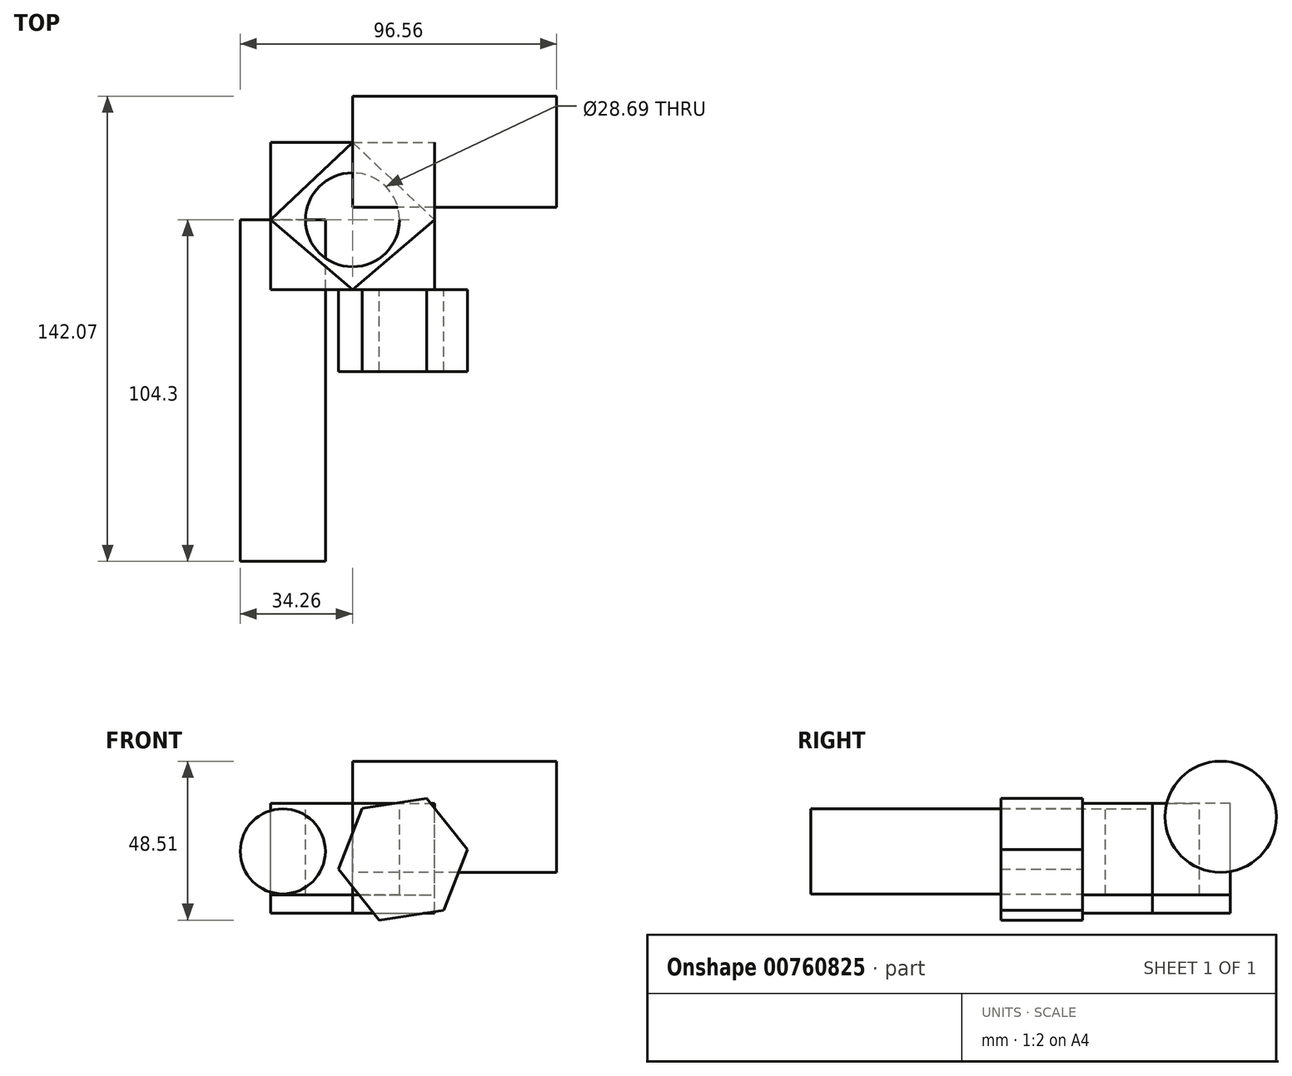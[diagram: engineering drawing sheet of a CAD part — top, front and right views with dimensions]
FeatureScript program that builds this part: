
annotation { "Feature Type Name" : "Feature", "Feature Type Description" : "" }
export const myFeature = defineFeature(function(context is Context, id is Id, definition is map)
    precondition{}
    {
        {
            var Q0;
            Q0=qCreatedBy(makeId("Top.planeOp"),FACE);
            var sketch = newSketch(context, id + "F0", { "sketchPlane" : qUnion([Q0])});
            skLineSegment(sketch, "E0.bottom", {"start": v(-25, 23.69) * mm, "end": v(25, 23.69) * mm});
            skLineSegment(sketch, "E0.top", {"start": v(-25, -21.31) * mm, "end": v(25, -21.31) * mm});
            skLineSegment(sketch, "E0.left", {"start": v(-25, 23.69) * mm, "end": v(-25, -21.31) * mm});
            skLineSegment(sketch, "E0.right", {"start": v(25, 23.69) * mm, "end": v(25, -21.31) * mm});
            skLineSegment(sketch, "E1", {"start": v(0, 23.69) * mm, "end": v(-25, 0) * mm});
            skLineSegment(sketch, "E2", {"start": v(-25, 0) * mm, "end": v(0, -21.31) * mm});
            skLineSegment(sketch, "E3", {"start": v(0, -21.31) * mm, "end": v(25, 0) * mm});
            skLineSegment(sketch, "E4", {"start": v(0, 23.69) * mm, "end": v(25, 0) * mm});
            skCircle(sketch, "E5", {"center": v(0, 0) * mm, "radius": 14.35 * mm});
            skSolve(sketch);
        }
        {
            var Q0;
            {var subQ3=sQuery(id+"F0.wireOp",EDGE,"E1");Q0=makeQuery(id+"F0.imprint","IMPRINT",FACE,{"disambiguationData":[TD([[makeQuery(id+"F0.imprint","IMPRINT",EDGE,{"derivedFrom":subQ3}),-1.0]])]});}
            var Q1;
            {var subQ3=sQuery(id+"F0.wireOp",EDGE,"E4");Q1=makeQuery(id+"F0.imprint","IMPRINT",FACE,{"disambiguationData":[TD([[makeQuery(id+"F0.imprint","IMPRINT",EDGE,{"derivedFrom":subQ3}),1.0]])]});}
            var Q2;
            {var subQ3=sQuery(id+"F0.wireOp",EDGE,"E2");Q2=makeQuery(id+"F0.imprint","IMPRINT",FACE,{"disambiguationData":[TD([[makeQuery(id+"F0.imprint","IMPRINT",EDGE,{"derivedFrom":subQ3}),-1.0]])]});}
            var Q3;
            {var subQ3=sQuery(id+"F0.wireOp",EDGE,"E3");Q3=makeQuery(id+"F0.imprint","IMPRINT",FACE,{"disambiguationData":[TD([[makeQuery(id+"F0.imprint","IMPRINT",EDGE,{"derivedFrom":subQ3}),-1.0]])]});}
            extrude(context, id + "F1", {"entities" : qUnion([Q0, Q1, Q2, Q3]), "oppositeDirection" : true, "depth" : 33.6 * mm, "offsetDistance" : 25 * mm});
        }
        {
            var Q0;
            Q0 = qSketchRegion(id + "F0", true);
            extrude(context, id + "F2", {"entities" : qUnion([Q0]), "oppositeDirection" : true, "depth" : 27.9 * mm, "offsetDistance" : 25 * mm});
        }
        {
            var Q0;
            Q0=qCreatedBy(makeId("Right.planeOp"),FACE);
            var sketch = newSketch(context, id + "F3", { "sketchPlane" : qUnion([Q0])});
            skCircle(sketch, "E6", {"center": v(20.79, -4.12) * mm, "radius": 16.98 * mm});
            skSolve(sketch);
        }
        {
            var Q0;
            Q0 = qSketchRegion(id + "F3", true);
            extrude(context, id + "F4", {"entities" : qUnion([Q0]), "depth" : 62.3 * mm, "offsetDistance" : 25 * mm});
        }
        {
            var Q0;
            Q0=qCreatedBy(makeId("Front.planeOp"),FACE);
            var sketch = newSketch(context, id + "F5", { "sketchPlane" : qUnion([Q0])});
            skCircle(sketch, "E7", {"center": v(-21.27, -14.66) * mm, "radius": 12.99 * mm});
            skSolve(sketch);
        }
        {
            var Q0;
            Q0 = qSketchRegion(id + "F5", true);
            extrude(context, id + "F6", {"entities" : qUnion([Q0]), "depth" : 104.3 * mm, "offsetDistance" : 25 * mm});
        }
        {
            var Q0;
            Q0=makeQuery(id+"F2.opExtrude","SWEPT_FACE",FACE,{"disambiguationData":[OSD([sQuery(id+"F0.wireOp",EDGE,"E0.top")])]});
            var sketch = newSketch(context, id + "F7", { "sketchPlane" : qUnion([Q0])});
            skCircle(sketch, "E8.cCircle", {"center": v(15.4, -17.07) * mm, "radius": 17.27 * mm, "construction": true});
            skLineSegment(sketch, "E8.0", {"start": v(2.93, -1.5) * mm, "end": v(22.65, 1.5) * mm});
            skLineSegment(sketch, "E8.1", {"start": v(22.65, 1.5) * mm, "end": v(35.1, -14.07) * mm});
            skLineSegment(sketch, "E8.2", {"start": v(35.1, -14.07) * mm, "end": v(27.86, -32.64) * mm});
            skLineSegment(sketch, "E8.3", {"start": v(27.86, -32.64) * mm, "end": v(8.14, -35.65) * mm});
            skLineSegment(sketch, "E8.4", {"start": v(8.14, -35.65) * mm, "end": v(-4.32, -20.08) * mm});
            skLineSegment(sketch, "E8.5", {"start": v(-4.32, -20.08) * mm, "end": v(2.93, -1.5) * mm});
            skPoint(sketch, "E8.0.midPoint", {"position": v(12.8, 0) * mm});
            skSolve(sketch);
        }
        {
            var Q0;
            Q0 = qSketchRegion(id + "F7", true);
            extrude(context, id + "F8", {"entities" : qUnion([Q0]), "depth" : 25 * mm, "offsetDistance" : 25 * mm});
        }
    });
